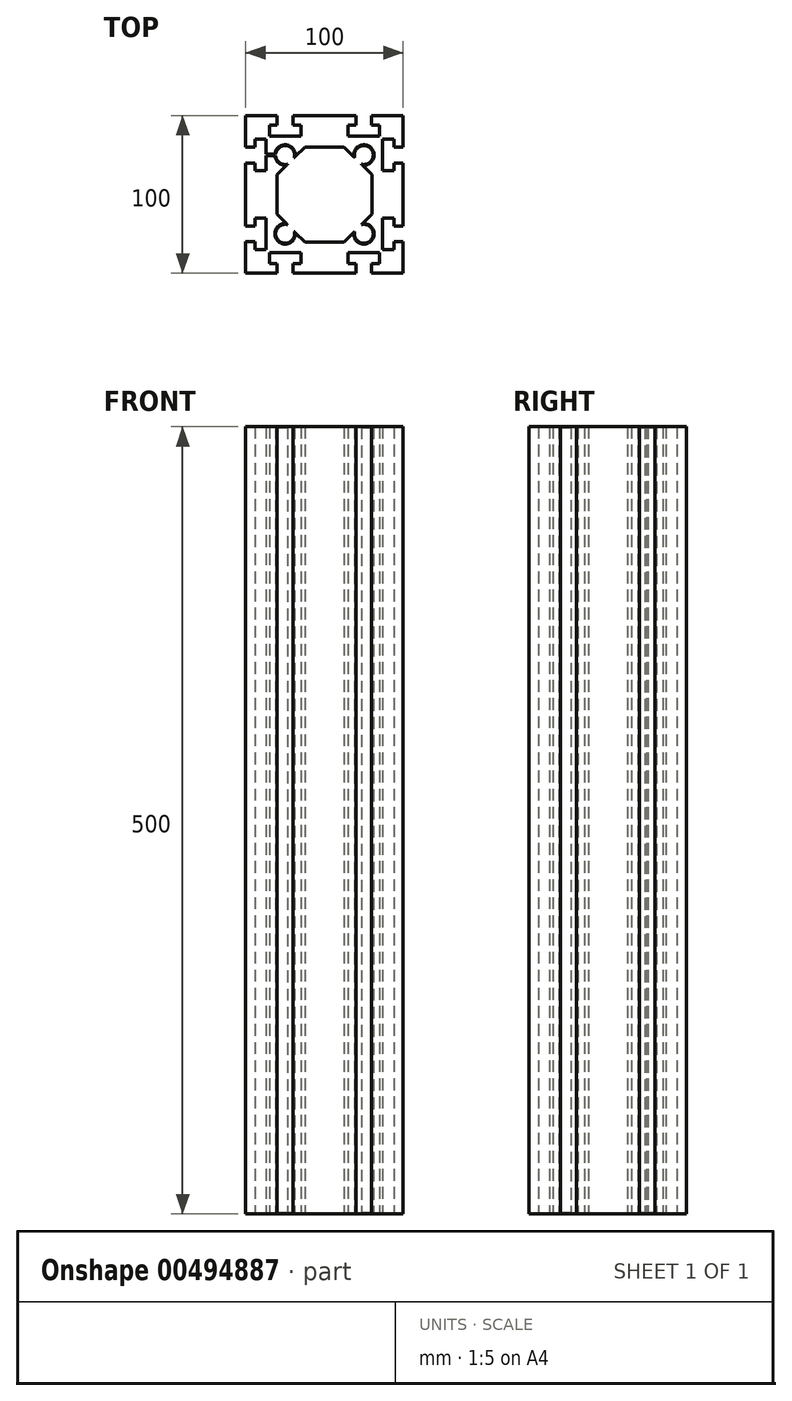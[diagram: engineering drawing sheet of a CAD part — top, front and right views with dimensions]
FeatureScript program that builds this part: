
annotation { "Feature Type Name" : "Feature", "Feature Type Description" : "" }
export const myFeature = defineFeature(function(context is Context, id is Id, definition is map)
    precondition{}
    {
        {
            var Q0;
            Q0=qCreatedBy(makeId("Top.planeOp"),FACE);
            var sketch = newSketch(context, id + "F0", { "sketchPlane" : qUnion([Q0])});
            skLineSegment(sketch, "E0.bottom", {"start": v(-50, 50) * mm, "end": v(-30, 50) * mm});
            skLineSegment(sketch, "E0.left", {"start": v(-50, 50) * mm, "end": v(-50, 30) * mm});
            skArc(sketch, "E1", {"start": v(-19.2, 23.48) * mm, "mid": v(-20.4, 28.86) * mm, "end": v(-25.5, 30.98) * mm});
            skArc(sketch, "E2", {"start": v(23.48, 19.2) * mm, "mid": v(29.24, 29.24) * mm, "end": v(19.2, 23.48) * mm});
            skArc(sketch, "E3", {"start": v(19.2, -23.48) * mm, "mid": v(29.24, -29.24) * mm, "end": v(23.48, -19.2) * mm});
            skArc(sketch, "E4", {"start": v(-23.48, -19.2) * mm, "mid": v(-29.24, -29.24) * mm, "end": v(-19.2, -23.48) * mm});
            skLineSegment(sketch, "E5.bottom", {"start": v(-44, 35) * mm, "end": v(-37, 35) * mm});
            skLineSegment(sketch, "E5.top", {"start": v(-44, 15) * mm, "end": v(-37, 15) * mm});
            skLineSegment(sketch, "E5.left", {"start": v(-44, 35) * mm, "end": v(-44, 30) * mm});
            skLineSegment(sketch, "E5.right", {"start": v(-37, 35) * mm, "end": v(-37, 25.5) * mm});
            skLineSegment(sketch, "E6", {"start": v(-44, 30) * mm, "end": v(-50, 30) * mm});
            skLineSegment(sketch, "E7", {"start": v(-44, 20) * mm, "end": v(-50, 20) * mm});
            skLineSegment(sketch, "E8.trimOffspring", {"start": v(-44, 20) * mm, "end": v(-44, 15) * mm});
            skLineSegment(sketch, "E9.1.0.0", {"start": v(-44, -35) * mm, "end": v(-37, -35) * mm});
            skLineSegment(sketch, "E9.1.0.1", {"start": v(-44, -15) * mm, "end": v(-37, -15) * mm});
            skLineSegment(sketch, "E9.1.0.2", {"start": v(-37, -15) * mm, "end": v(-37, -35) * mm});
            skLineSegment(sketch, "E9.1.0.3", {"start": v(-44, -15) * mm, "end": v(-44, -20) * mm});
            skLineSegment(sketch, "E9.1.0.4", {"start": v(-44, -20) * mm, "end": v(-50, -20) * mm});
            skLineSegment(sketch, "E9.1.0.5", {"start": v(-44, -30) * mm, "end": v(-44, -35) * mm});
            skLineSegment(sketch, "E9.1.0.6", {"start": v(-44, -30) * mm, "end": v(-50, -30) * mm});
            skLineSegment(sketch, "E10", {"start": v(-50, 20) * mm, "end": v(-50, -20) * mm});
            skLineSegment(sketch, "E11", {"start": v(-50, -30) * mm, "end": v(-50, -50) * mm});
            skLineSegment(sketch, "E12.bottom", {"start": v(-35, 44) * mm, "end": v(-30, 44) * mm});
            skLineSegment(sketch, "E12.top", {"start": v(-35, 37) * mm, "end": v(-25.5, 37) * mm});
            skLineSegment(sketch, "E12.left", {"start": v(-35, 44) * mm, "end": v(-35, 37) * mm});
            skLineSegment(sketch, "E12.right", {"start": v(-15, 44) * mm, "end": v(-15, 37) * mm});
            skLineSegment(sketch, "E13.left", {"start": v(-30, 50) * mm, "end": v(-30, 44) * mm});
            skLineSegment(sketch, "E13.right", {"start": v(-20, 50) * mm, "end": v(-20, 44) * mm});
            skLineSegment(sketch, "E14.trimOffspring", {"start": v(-20, 44) * mm, "end": v(-15, 44) * mm});
            skLineSegment(sketch, "E15.trimOffspring", {"start": v(-20, 50) * mm, "end": v(20, 50) * mm});
            skLineSegment(sketch, "E16.1.0.0", {"start": v(15, 44) * mm, "end": v(15, 37) * mm});
            skLineSegment(sketch, "E16.1.0.1", {"start": v(15, 44) * mm, "end": v(20, 44) * mm});
            skLineSegment(sketch, "E16.1.0.2", {"start": v(20, 50) * mm, "end": v(20, 44) * mm});
            skLineSegment(sketch, "E16.1.0.3", {"start": v(30, 44) * mm, "end": v(35, 44) * mm});
            skLineSegment(sketch, "E16.1.0.4", {"start": v(30, 50) * mm, "end": v(30, 44) * mm});
            skLineSegment(sketch, "E16.1.0.5", {"start": v(35, 44) * mm, "end": v(35, 37) * mm});
            skLineSegment(sketch, "E16.1.0.6", {"start": v(15, 37) * mm, "end": v(35, 37) * mm});
            skLineSegment(sketch, "E17.trimOffspring", {"start": v(30, 50) * mm, "end": v(50, 50) * mm});
            skLineSegment(sketch, "E18.MirrorCS", {"start": v(44, -30) * mm, "end": v(44, -35) * mm});
            skLineSegment(sketch, "E19.MirrorCS", {"start": v(44, -15) * mm, "end": v(44, -20) * mm});
            skLineSegment(sketch, "E20.MirrorCS", {"start": v(44, 30) * mm, "end": v(50, 30) * mm});
            skLineSegment(sketch, "E21.MirrorCS", {"start": v(44, 20) * mm, "end": v(50, 20) * mm});
            skLineSegment(sketch, "E22.MirrorCS", {"start": v(44, -30) * mm, "end": v(50, -30) * mm});
            skLineSegment(sketch, "E23.MirrorCS", {"start": v(44, -20) * mm, "end": v(50, -20) * mm});
            skLineSegment(sketch, "E24.MirrorCS", {"start": v(44, 35) * mm, "end": v(37, 35) * mm});
            skLineSegment(sketch, "E25.MirrorCS", {"start": v(44, 35) * mm, "end": v(44, 30) * mm});
            skLineSegment(sketch, "E26.MirrorCS", {"start": v(44, 20) * mm, "end": v(44, 15) * mm});
            skLineSegment(sketch, "E27.MirrorCS", {"start": v(37, 35) * mm, "end": v(37, 15) * mm});
            skLineSegment(sketch, "E28.MirrorCS", {"start": v(44, 15) * mm, "end": v(37, 15) * mm});
            skLineSegment(sketch, "E29.MirrorCS", {"start": v(37, -15) * mm, "end": v(37, -35) * mm});
            skLineSegment(sketch, "E30.MirrorCS", {"start": v(44, -15) * mm, "end": v(37, -15) * mm});
            skLineSegment(sketch, "E31.MirrorCS", {"start": v(44, -35) * mm, "end": v(37, -35) * mm});
            skLineSegment(sketch, "E32", {"start": v(50, 50) * mm, "end": v(50, 30) * mm});
            skLineSegment(sketch, "E33", {"start": v(50, 20) * mm, "end": v(50, -20) * mm});
            skLineSegment(sketch, "E34", {"start": v(50, -30) * mm, "end": v(50, -50) * mm});
            skLineSegment(sketch, "E35.MirrorCS", {"start": v(-35, -44) * mm, "end": v(-35, -37) * mm});
            skLineSegment(sketch, "E36.MirrorCS", {"start": v(-20, -50) * mm, "end": v(-20, -44) * mm});
            skLineSegment(sketch, "E37.MirrorCS", {"start": v(-30, -50) * mm, "end": v(-30, -44) * mm});
            skLineSegment(sketch, "E38.MirrorCS", {"start": v(30, -44) * mm, "end": v(35, -44) * mm});
            skLineSegment(sketch, "E39.MirrorCS", {"start": v(20, -50) * mm, "end": v(20, -44) * mm});
            skLineSegment(sketch, "E40.MirrorCS", {"start": v(35, -44) * mm, "end": v(35, -37) * mm});
            skLineSegment(sketch, "E41.MirrorCS", {"start": v(15, -44) * mm, "end": v(15, -37) * mm});
            skLineSegment(sketch, "E42.MirrorCS", {"start": v(15, -44) * mm, "end": v(20, -44) * mm});
            skLineSegment(sketch, "E43.MirrorCS", {"start": v(-20, -44) * mm, "end": v(-15, -44) * mm});
            skLineSegment(sketch, "E44.MirrorCS", {"start": v(30, -50) * mm, "end": v(30, -44) * mm});
            skLineSegment(sketch, "E45.MirrorCS", {"start": v(-15, -44) * mm, "end": v(-15, -37) * mm});
            skLineSegment(sketch, "E46.MirrorCS", {"start": v(-35, -44) * mm, "end": v(-30, -44) * mm});
            skLineSegment(sketch, "E47.MirrorCS", {"start": v(-50, -50) * mm, "end": v(-30, -50) * mm});
            skLineSegment(sketch, "E48.MirrorCS", {"start": v(30, -50) * mm, "end": v(50, -50) * mm});
            skLineSegment(sketch, "E49.MirrorCS", {"start": v(-35, -37) * mm, "end": v(-15, -37) * mm});
            skLineSegment(sketch, "E50.MirrorCS", {"start": v(-20, -50) * mm, "end": v(20, -50) * mm});
            skLineSegment(sketch, "E51.MirrorCS", {"start": v(15, -37) * mm, "end": v(35, -37) * mm});
            skLineSegment(sketch, "E52", {"start": v(12.5, 30.18) * mm, "end": v(19.2, 23.48) * mm});
            skLineSegment(sketch, "E53", {"start": v(30.18, 12.5) * mm, "end": v(30.18, -12.5) * mm});
            skLineSegment(sketch, "E54", {"start": v(30.18, -12.5) * mm, "end": v(23.48, -19.2) * mm});
            skLineSegment(sketch, "E55", {"start": v(12.5, -30.18) * mm, "end": v(-12.5, -30.18) * mm});
            skLineSegment(sketch, "E56", {"start": v(-12.5, -30.18) * mm, "end": v(-19.2, -23.48) * mm});
            skLineSegment(sketch, "E57", {"start": v(-30.18, -12.5) * mm, "end": v(-30.18, 12.5) * mm});
            skLineSegment(sketch, "E58", {"start": v(-30.18, 12.5) * mm, "end": v(-23.48, 19.2) * mm});
            skLineSegment(sketch, "E59", {"start": v(-12.5, 30.18) * mm, "end": v(12.5, 30.18) * mm});
            skLineSegment(sketch, "E60", {"start": v(0, 0) * mm, "end": v(-30.18, 0) * mm, "construction": true});
            skLineSegment(sketch, "E61", {"start": v(0, 0) * mm, "end": v(30.18, 0) * mm, "construction": true});
            skLineSegment(sketch, "E62", {"start": v(0, 0) * mm, "end": v(0, 30.18) * mm, "construction": true});
            skLineSegment(sketch, "E63", {"start": v(0, 0) * mm, "end": v(0, -30.18) * mm, "construction": true});
            skLineSegment(sketch, "E64.trimOffspring", {"start": v(-23.48, -19.2) * mm, "end": v(-30.18, -12.5) * mm});
            skLineSegment(sketch, "E65.trimOffspring", {"start": v(19.2, -23.48) * mm, "end": v(12.5, -30.18) * mm});
            skLineSegment(sketch, "E66.trimOffspring", {"start": v(23.48, 19.2) * mm, "end": v(30.18, 12.5) * mm});
            skLineSegment(sketch, "E67.trimOffspring", {"start": v(-19.2, 23.48) * mm, "end": v(-12.5, 30.18) * mm});
            skLineSegment(sketch, "E68", {"start": v(-37, 25.5) * mm, "end": v(-30.98, 25.5) * mm});
            skLineSegment(sketch, "E69", {"start": v(-30.98, 24.5) * mm, "end": v(-37, 24.5) * mm});
            skPoint(sketch, "E69.endSnap0", {"position": v(-37, 25) * mm});
            skArc(sketch, "E70.trimOffspring", {"start": v(-30.98, 24.5) * mm, "mid": v(-28.47, 20.1) * mm, "end": v(-23.48, 19.2) * mm});
            skLineSegment(sketch, "E71.trimOffspring", {"start": v(-37, 24.5) * mm, "end": v(-37, 15) * mm});
            skArc(sketch, "E72.trimOffspring", {"start": v(-25.5, 30.98) * mm, "mid": v(-29.24, 29.24) * mm, "end": v(-30.98, 25.5) * mm});
            skLineSegment(sketch, "E73.trimOffspring", {"start": v(-25.5, 37) * mm, "end": v(-15, 37) * mm});
            skSolve(sketch);
        }
        {
            var Q0;
            Q0=qSketchRegion(id+"F0",true);
            extrude(context, id + "F1", {"entities" : qUnion([Q0]), "depth" : 500 * mm});
        }
        {
            var Q0;
            Q0=makeQuery(id+"F1.opExtrude","CAP_EDGE",EDGE,{"disambiguationData":[OSD([sQuery(id+"F0.wireOp",EDGE,"E1"),sQuery(id+"F0.wireOp",EDGE,"E72.trimOffspring")])],"isStart":false});
            var Q1;
            Q1=makeQuery(id+"F1.opExtrude","CAP_EDGE",EDGE,{"disambiguationData":[OSD([sQuery(id+"F0.wireOp",EDGE,"E70.trimOffspring")])],"isStart":false});
            var Q2;
            Q2=makeQuery(id+"F1.opExtrude","CAP_EDGE",EDGE,{"disambiguationData":[OSD([sQuery(id+"F0.wireOp",EDGE,"E4")])],"isStart":false});
            var Q3;
            Q3=makeQuery(id+"F1.opExtrude","CAP_EDGE",EDGE,{"disambiguationData":[OSD([sQuery(id+"F0.wireOp",EDGE,"E3")])],"isStart":false});
            var Q4;
            Q4=makeQuery(id+"F1.opExtrude","CAP_EDGE",EDGE,{"disambiguationData":[OSD([sQuery(id+"F0.wireOp",EDGE,"E2")])],"isStart":false});
            var Q5;
            Q5=makeQuery(id+"F1.opExtrude","CAP_EDGE",EDGE,{"disambiguationData":[OSD([sQuery(id+"F0.wireOp",EDGE,"E2")])],"isStart":true});
            var Q6;
            Q6=makeQuery(id+"F1.opExtrude","CAP_EDGE",EDGE,{"disambiguationData":[OSD([sQuery(id+"F0.wireOp",EDGE,"E3")])],"isStart":true});
            var Q7;
            Q7=makeQuery(id+"F1.opExtrude","CAP_EDGE",EDGE,{"disambiguationData":[OSD([sQuery(id+"F0.wireOp",EDGE,"E4")])],"isStart":true});
            var Q8;
            Q8=makeQuery(id+"F1.opExtrude","CAP_EDGE",EDGE,{"disambiguationData":[OSD([sQuery(id+"F0.wireOp",EDGE,"E70.trimOffspring")])],"isStart":true});
            var Q9;
            Q9=makeQuery(id+"F1.opExtrude","CAP_EDGE",EDGE,{"disambiguationData":[OSD([sQuery(id+"F0.wireOp",EDGE,"E1"),sQuery(id+"F0.wireOp",EDGE,"E72.trimOffspring")])],"isStart":true});
            chamfer(context, id + "F2", {"entities" : qUnion([Q0, Q1, Q2, Q3, Q4, Q5, Q6, Q7, Q8, Q9]), "width" : 0.5 * mm, "tangentPropagation" : true});
        }
    });
